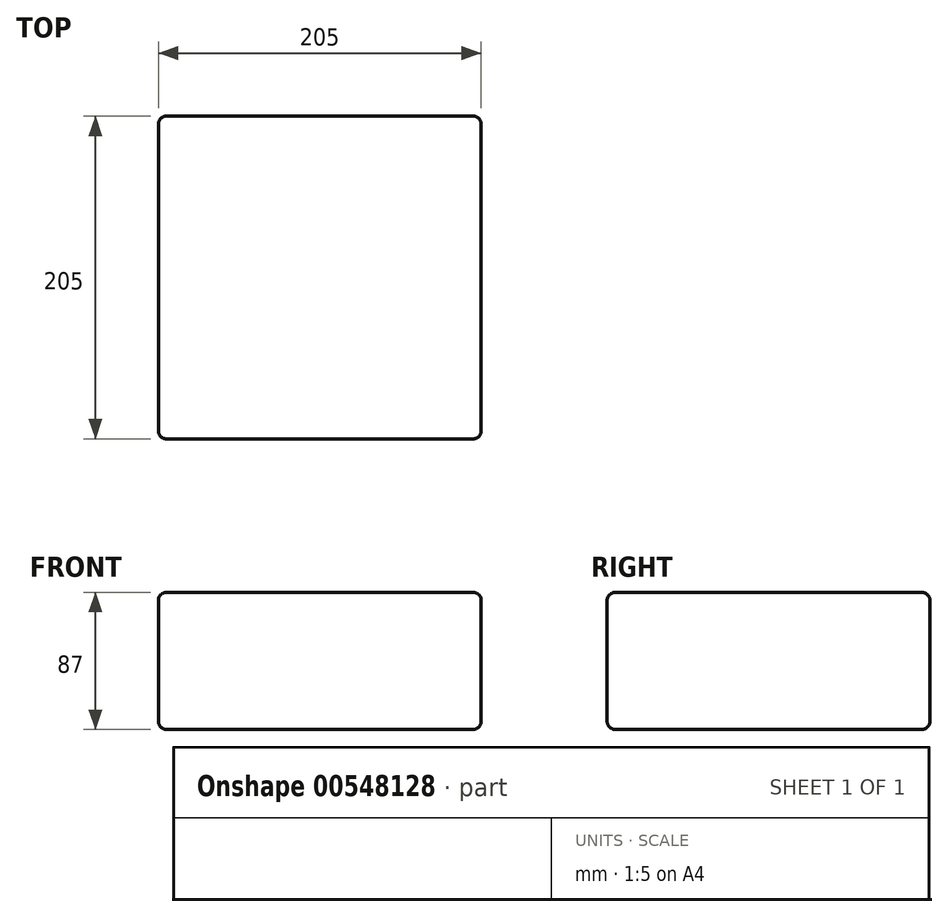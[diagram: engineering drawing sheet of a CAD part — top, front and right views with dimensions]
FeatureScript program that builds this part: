
annotation { "Feature Type Name" : "Feature", "Feature Type Description" : "" }
export const myFeature = defineFeature(function(context is Context, id is Id, definition is map)
    precondition{}
    {
        {
            var Q0;
            Q0=qCreatedBy(makeId("Top.planeOp"),FACE);
            var sketch = newSketch(context, id + "F0", { "sketchPlane" : qUnion([Q0])});
            skLineSegment(sketch, "E0.bottom", {"start": v(0, 0) * mm, "end": v(0, 0) * mm});
            skLineSegment(sketch, "E0.top", {"start": v(0, 23.49) * mm, "end": v(0, 23.49) * mm});
            skLineSegment(sketch, "E0.left", {"start": v(0, 0) * mm, "end": v(0, 23.49) * mm});
            skLineSegment(sketch, "E0.right", {"start": v(0, 0) * mm, "end": v(0, 23.49) * mm});
            skLineSegment(sketch, "E1.bottom", {"start": v(0, 0) * mm, "end": v(-205, 0) * mm});
            skLineSegment(sketch, "E1.top", {"start": v(0, 205) * mm, "end": v(-205, 205) * mm});
            skLineSegment(sketch, "E1.left", {"start": v(0, 0) * mm, "end": v(0, 205) * mm});
            skLineSegment(sketch, "E1.right", {"start": v(-205, 0) * mm, "end": v(-205, 205) * mm});
            skSolve(sketch);
        }
        {
            var Q0;
            {var subQ0=sQuery(id+"F0.wireOp",EDGE,"E1.bottom");Q0=makeQuery(id+"F0.imprint","IMPRINT",FACE,{"disambiguationData":[TD([[makeQuery(id+"F0.imprint","IMPRINT",EDGE,{"derivedFrom":subQ0}),-1.0]])]});}
            extrude(context, id + "F1", {"entities" : qUnion([Q0]), "depth" : 87 * mm, "offsetDistance" : 25 * mm});
        }
        {
            var Q0;
            Q0=makeQuery(id+"F1.opExtrude","SWEPT_FACE",FACE,{"disambiguationData":[OSD([sQuery(id+"F0.wireOp",EDGE,"E1.bottom")])]});
            var Q1;
            Q1=makeQuery(id+"F1.opExtrude","CAP_FACE",FACE,{"disambiguationData":[OSD([sQuery(id+"F0.wireOp",EDGE,"E1.bottom"),sQuery(id+"F0.wireOp",EDGE,"E1.top"),sQuery(id+"F0.wireOp",EDGE,"E1.left"),sQuery(id+"F0.wireOp",EDGE,"E1.right")])],"isStart":false});
            var Q2;
            Q2=makeQuery(id+"F1.opExtrude","SWEPT_FACE",FACE,{"disambiguationData":[OSD([sQuery(id+"F0.wireOp",EDGE,"E1.left")])]});
            var Q3;
            Q3=makeQuery(id+"F1.opExtrude","SWEPT_FACE",FACE,{"disambiguationData":[OSD([sQuery(id+"F0.wireOp",EDGE,"E1.right")])]});
            var Q4;
            Q4=makeQuery(id+"F1.opExtrude","CAP_FACE",FACE,{"disambiguationData":[OSD([sQuery(id+"F0.wireOp",EDGE,"E1.bottom"),sQuery(id+"F0.wireOp",EDGE,"E1.top"),sQuery(id+"F0.wireOp",EDGE,"E1.left"),sQuery(id+"F0.wireOp",EDGE,"E1.right")])],"isStart":true});
            fillet(context, id + "F2", {"entities" : qUnion([Q0, Q1, Q2, Q3, Q4]), "radius" : 5 * mm, "tangentPropagation" : true, "allowEdgeOverflow" : false});
        }
    });
